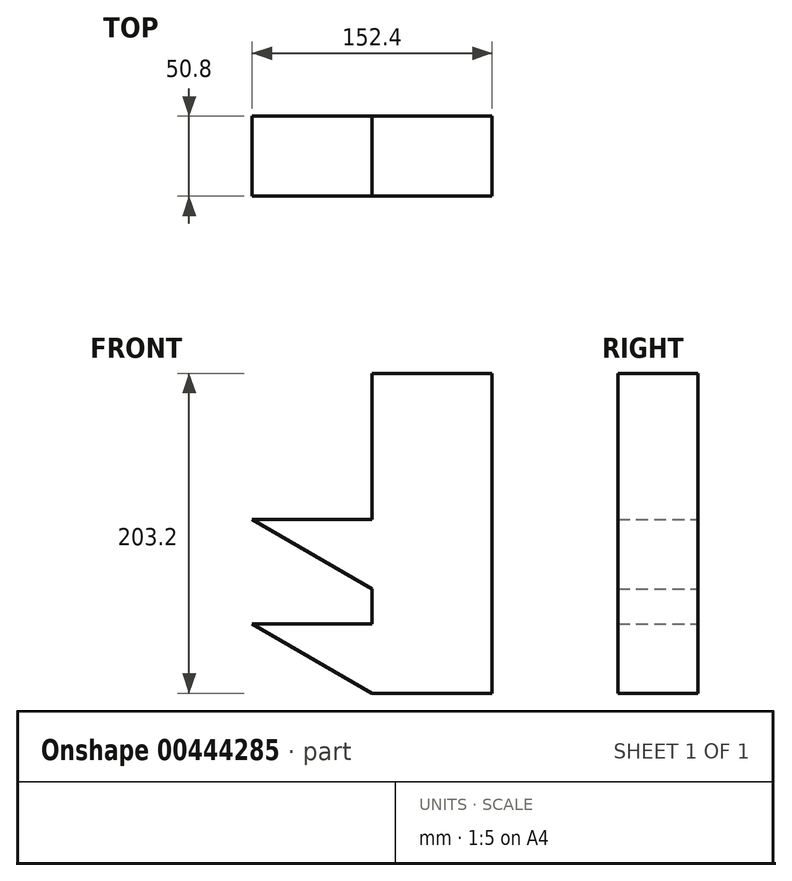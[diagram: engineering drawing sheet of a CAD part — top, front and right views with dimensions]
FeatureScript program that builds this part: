
annotation { "Feature Type Name" : "Feature", "Feature Type Description" : "" }
export const myFeature = defineFeature(function(context is Context, id is Id, definition is map)
    precondition{}
    {
        {
            var Q0;
            Q0=qCreatedBy(makeId("Front.planeOp"),FACE);
            var sketch = newSketch(context, id + "F0", { "sketchPlane" : qUnion([Q0])});
            skLineSegment(sketch, "E0.bottom", {"start": v(0, -101.6) * mm, "end": v(76.2, -101.6) * mm});
            skLineSegment(sketch, "E0.top", {"start": v(0, 101.6) * mm, "end": v(76.2, 101.6) * mm});
            skLineSegment(sketch, "E0.left", {"start": v(0, -101.6) * mm, "end": v(0, 101.6) * mm});
            skLineSegment(sketch, "E0.right", {"start": v(76.2, -101.6) * mm, "end": v(76.2, 101.6) * mm});
            skPoint(sketch, "E0.middle", {"position": v(38.1, 0) * mm});
            skLineSegment(sketch, "E1", {"start": v(0, -101.6) * mm, "end": v(-76.2, -57.6) * mm});
            skLineSegment(sketch, "E2", {"start": v(-76.2, -57.6) * mm, "end": v(0, -57.6) * mm});
            skLineSegment(sketch, "E3", {"start": v(0, -57.6) * mm, "end": v(76.2, -101.6) * mm});
            skLineSegment(sketch, "E4", {"start": v(-76.2, 8.69) * mm, "end": v(0, -35.3) * mm});
            skLineSegment(sketch, "E5", {"start": v(-76.2, 8.69) * mm, "end": v(0, 8.69) * mm});
            skLineSegment(sketch, "E6", {"start": v(0, 8.69) * mm, "end": v(0, -35.3) * mm});
            skSolve(sketch);
        }
        {
            var Q0;
            {var subQ1=sQuery(id+"F0.wireOp",EDGE,"E0.top");Q0=makeQuery(id+"F0.imprint","IMPRINT",FACE,{"disambiguationData":[TD([[makeQuery(id+"F0.imprint","IMPRINT",EDGE,{"derivedFrom":subQ1}),-1.0]])]});}
            var Q1;
            {var subQ0=sQuery(id+"F0.wireOp",EDGE,"E0.bottom");Q1=makeQuery(id+"F0.imprint","IMPRINT",FACE,{"disambiguationData":[TD([[makeQuery(id+"F0.imprint","IMPRINT",EDGE,{"derivedFrom":subQ0}),1.0]])]});}
            var Q2;
            {var subQ0=sQuery(id+"F0.wireOp",EDGE,"E1");Q2=makeQuery(id+"F0.imprint","IMPRINT",FACE,{"disambiguationData":[TD([[makeQuery(id+"F0.imprint","IMPRINT",EDGE,{"derivedFrom":subQ0}),-1.0]])]});}
            var Q3;
            Q3=makeQuery(id+"F0.imprint","IMPRINT",FACE,{"disambiguationData":[TD([[makeQuery(id+"F0.imprint","IMPRINT",EDGE,{"derivedFrom":sQuery(id+"F0.wireOp",EDGE,"E4")}),1.0]])]});
            extrude(context, id + "F1", {"entities" : qUnion([Q0, Q1, Q2, Q3]), "depth" : 25.4 * mm, "hasSecondDirection" : true, "secondDirectionOppositeDirection" : true, "secondDirectionDepth" : 25.4 * mm});
        }
    });
